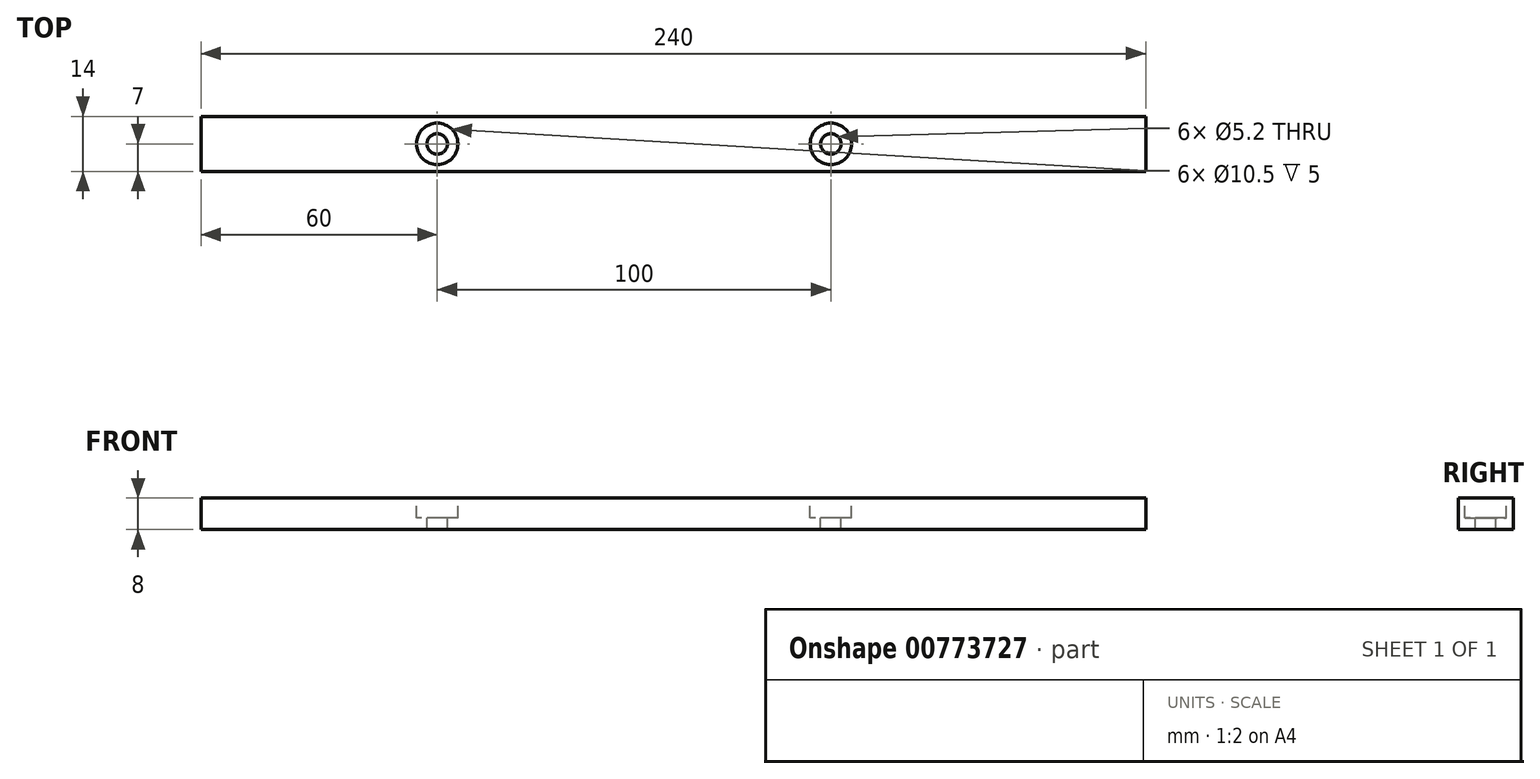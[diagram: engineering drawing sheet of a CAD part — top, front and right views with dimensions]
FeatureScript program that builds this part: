
annotation { "Feature Type Name" : "Feature", "Feature Type Description" : "" }
export const myFeature = defineFeature(function(context is Context, id is Id, definition is map)
    precondition{}
    {
        {
            var Q0;
            Q0=qCreatedBy(makeId("Top.planeOp"),FACE);
            var sketch = newSketch(context, id + "F0", { "sketchPlane" : qUnion([Q0])});
            skLineSegment(sketch, "E0", {"start": v(0, 0) * mm, "end": v(0, 113.27) * mm, "construction": true});
            skLineSegment(sketch, "E1.bottom", {"start": v(120, -7) * mm, "end": v(-120, -7) * mm});
            skLineSegment(sketch, "E1.top", {"start": v(120, 7) * mm, "end": v(-120, 7) * mm});
            skLineSegment(sketch, "E1.left", {"start": v(120, -7) * mm, "end": v(120, 7) * mm});
            skLineSegment(sketch, "E1.right", {"start": v(-120, -7) * mm, "end": v(-120, 7) * mm});
            skPoint(sketch, "E1.middle", {"position": v(0, 0) * mm});
            skSolve(sketch);
        }
        {
            var Q0;
            Q0 = qSketchRegion(id + "F0", true);
            extrude(context, id + "F1", {"entities" : qUnion([Q0]), "depth" : 8 * mm, "offsetDistance" : 25 * mm});
        }
        {
            var Q0;
            Q0=makeQuery(id+"F1.opExtrude","CAP_FACE",FACE,{"disambiguationData":[OSD([sQuery(id+"F0.wireOp",EDGE,"E1.bottom"),sQuery(id+"F0.wireOp",EDGE,"E1.top"),sQuery(id+"F0.wireOp",EDGE,"E1.left"),sQuery(id+"F0.wireOp",EDGE,"E1.right")])],"isStart":false});
            var sketch = newSketch(context, id + "F2", { "sketchPlane" : qUnion([Q0])});
            skLineSegment(sketch, "E2", {"start": v(-120, 0) * mm, "end": v(120, 0) * mm, "construction": true});
            skPoint(sketch, "E3", {"position": v(-60, 0) * mm});
            skPoint(sketch, "E4", {"position": v(40, 0) * mm});
            skCircle(sketch, "E5", {"center": v(-60, 0) * mm, "radius": 5.25 * mm});
            skCircle(sketch, "E6", {"center": v(40, 0) * mm, "radius": 5.25 * mm});
            skCircle(sketch, "E7", {"center": v(-60, 0) * mm, "radius": 2.6 * mm});
            skCircle(sketch, "E8", {"center": v(40, 0) * mm, "radius": 2.6 * mm});
            skSolve(sketch);
        }
        {
            var Q0;
            Q0=makeQuery(id+"F2.imprint","IMPRINT",FACE,{"disambiguationData":[TD([[makeQuery(id+"F2.imprint","IMPRINT",EDGE,{"derivedFrom":sQuery(id+"F2.wireOp",EDGE,"E7")}),1.0]])]});
            var Q1;
            Q1=makeQuery(id+"F2.imprint","IMPRINT",FACE,{"disambiguationData":[TD([[makeQuery(id+"F2.imprint","IMPRINT",EDGE,{"derivedFrom":sQuery(id+"F2.wireOp",EDGE,"E8")}),1.0]])]});
            extrude(context, id + "F3", {"entities" : qUnion([Q0, Q1]), "operationType" : NewBodyOperationType.REMOVE, "endBound" : BoundingType.THROUGH_ALL, "oppositeDirection" : true, "depth" : 25 * mm, "offsetDistance" : 25 * mm});
        }
        {
            var Q0;
            Q0=makeQuery(id+"F2.imprint","IMPRINT",FACE,{"disambiguationData":[TD([[makeQuery(id+"F2.imprint","IMPRINT",EDGE,{"derivedFrom":sQuery(id+"F2.wireOp",EDGE,"E5")}),1.0]])]});
            var Q1;
            Q1=makeQuery(id+"F2.imprint","IMPRINT",FACE,{"disambiguationData":[TD([[makeQuery(id+"F2.imprint","IMPRINT",EDGE,{"derivedFrom":sQuery(id+"F2.wireOp",EDGE,"E6")}),1.0]])]});
            extrude(context, id + "F4", {"entities" : qUnion([Q0, Q1]), "operationType" : NewBodyOperationType.REMOVE, "oppositeDirection" : true, "depth" : 5 * mm, "offsetDistance" : 25 * mm});
        }
    });
